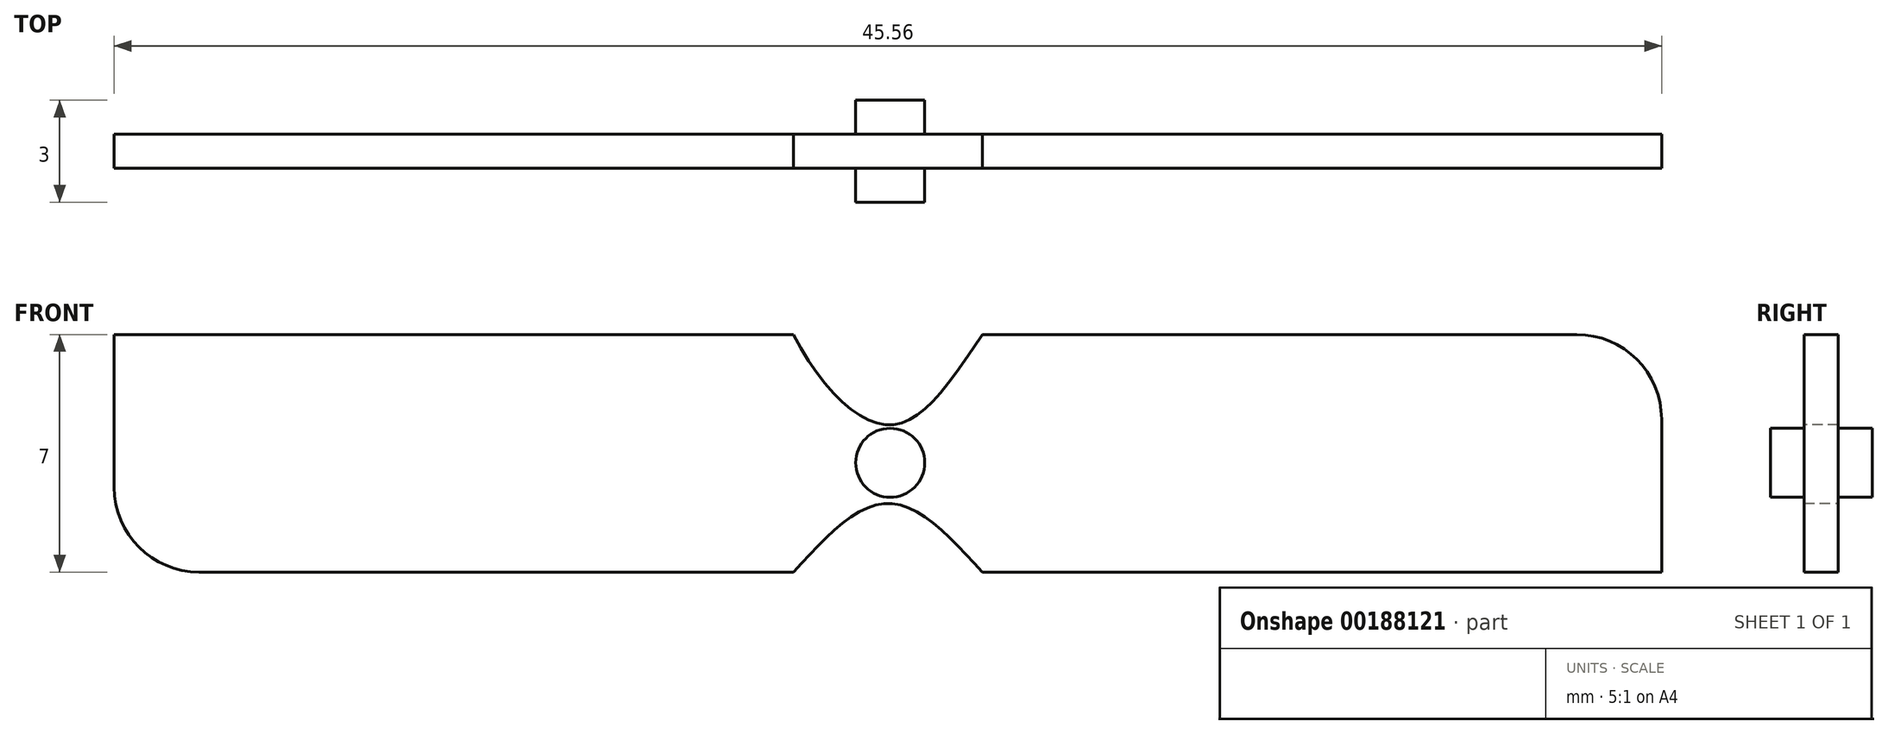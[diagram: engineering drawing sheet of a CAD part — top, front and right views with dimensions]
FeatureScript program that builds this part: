
annotation { "Feature Type Name" : "Feature", "Feature Type Description" : "" }
export const myFeature = defineFeature(function(context is Context, id is Id, definition is map)
    precondition{}
    {
        {
            var Q0;
            Q0=qCreatedBy(makeId("Front.planeOp"),FACE);
            var sketch = newSketch(context, id + "F0", { "sketchPlane" : qUnion([Q0])});
            skLineSegment(sketch, "E0.bottom", {"start": v(-20.53, 7) * mm, "end": v(-0.53, 7) * mm});
            skLineSegment(sketch, "E0.top", {"start": v(-18.03, 0) * mm, "end": v(-0.53, 0) * mm});
            skLineSegment(sketch, "E0.left", {"start": v(-20.53, 7) * mm, "end": v(-20.53, 2.5) * mm});
            skLineSegment(sketch, "E0.right", {"start": v(-0.53, 7) * mm, "end": v(-0.53, 0) * mm});
            skLineSegment(sketch, "E1.bottom", {"start": v(5.03, 7) * mm, "end": v(22.53, 7) * mm});
            skLineSegment(sketch, "E1.top", {"start": v(5.03, 0) * mm, "end": v(25.03, 0) * mm});
            skLineSegment(sketch, "E1.left", {"start": v(5.03, 7) * mm, "end": v(5.03, 0) * mm});
            skLineSegment(sketch, "E1.right", {"start": v(25.03, 4.5) * mm, "end": v(25.03, 0) * mm});
            skPoint(sketch, "E2.visualSharp", {"position": v(25.03, 7) * mm});
            skArc(sketch, "E2.filletArc", {"start": v(25.03, 4.5) * mm, "mid": v(24.3, 6.27) * mm, "end": v(22.53, 7) * mm});
            skPoint(sketch, "E3.visualSharp", {"position": v(-20.53, 0) * mm});
            skArc(sketch, "E3.filletArc", {"start": v(-20.53, 2.5) * mm, "mid": v(-19.8, 0.73) * mm, "end": v(-18.03, 0) * mm});
            skFitSpline(sketch, "E4", {"points": [v(-0.53, 7) * mm, v(2.32, 4.34) * mm, v(5.03, 7) * mm], "startDerivative": vector(4.9, -9.44) * mm, "endDerivative": vector(6.2, 9.3) * mm});
            skFitSpline(sketch, "E5", {"points": [v(-0.53, 0) * mm, v(2.25, 2.03) * mm, v(5.03, 0) * mm], "startDerivative": vector(5.56, 6.08) * mm, "endDerivative": vector(5.55, -6.08) * mm});
            skCircle(sketch, "E6", {"center": v(2.32, 3.22) * mm, "radius": 1.02 * mm});
            skSolve(sketch);
        }
        {
            var Q0;
            Q0=makeQuery(id+"F0.imprint","IMPRINT",FACE,{"disambiguationData":[TD([[makeQuery(id+"F0.imprint","IMPRINT",EDGE,{"derivedFrom":sQuery(id+"F0.wireOp",EDGE,"E1.bottom")}),-1.0]])]});
            var Q1;
            Q1=makeQuery(id+"F0.imprint","IMPRINT",FACE,{"disambiguationData":[TD([[makeQuery(id+"F0.imprint","IMPRINT",EDGE,{"derivedFrom":sQuery(id+"F0.wireOp",EDGE,"E0.bottom")}),-1.0]])]});
            var Q2;
            {var subQ4=sQuery(id+"F0.wireOp",EDGE,"E0.right");Q2=makeQuery(id+"F0.imprint","IMPRINT",FACE,{"disambiguationData":[TD([[makeQuery(id+"F0.imprint","IMPRINT",EDGE,{"derivedFrom":subQ4}),1.0]])]});}
            extrude(context, id + "F1", {"entities" : qUnion([Q0, Q1, Q2]), "depth" : 1 * mm});
        }
        {
            var Q0;
            Q0=makeQuery(id+"F0.imprint","IMPRINT",FACE,{"disambiguationData":[TD([[makeQuery(id+"F0.imprint","IMPRINT",EDGE,{"derivedFrom":sQuery(id+"F0.wireOp",EDGE,"E6")}),1.0]])]});
            extrude(context, id + "F2", {"entities" : qUnion([Q0]), "operationType" : NewBodyOperationType.ADD, "depth" : 2 * mm});
        }
        {
            var Q0;
            Q0=makeQuery(id+"F0.imprint","IMPRINT",FACE,{"disambiguationData":[TD([[makeQuery(id+"F0.imprint","IMPRINT",EDGE,{"derivedFrom":sQuery(id+"F0.wireOp",EDGE,"E6")}),1.0]])]});
            extrude(context, id + "F3", {"entities" : qUnion([Q0]), "operationType" : NewBodyOperationType.ADD, "oppositeDirection" : true, "depth" : 1 * mm});
        }
    });
